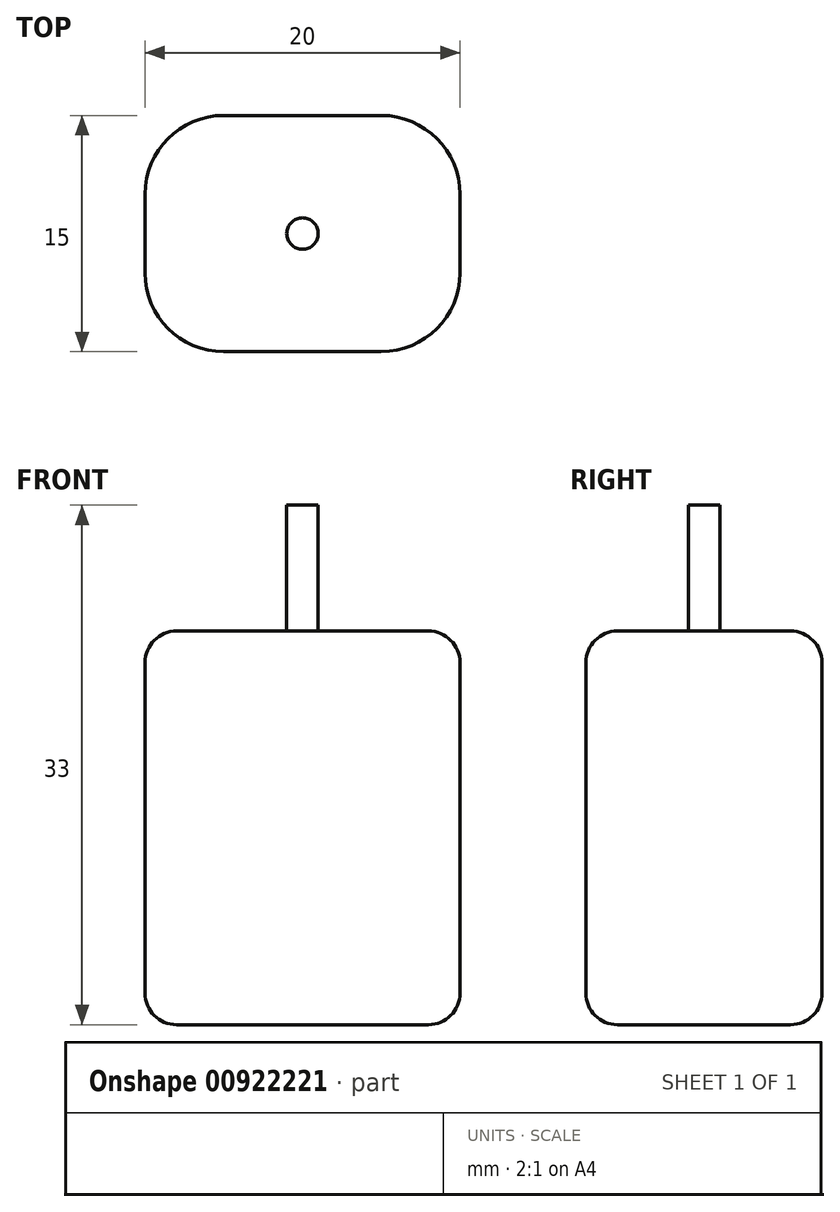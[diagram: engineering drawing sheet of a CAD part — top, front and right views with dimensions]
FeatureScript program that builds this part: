
annotation { "Feature Type Name" : "Feature", "Feature Type Description" : "" }
export const myFeature = defineFeature(function(context is Context, id is Id, definition is map)
    precondition{}
    {
        {
            var Q0;
            Q0=qCreatedBy(makeId("Top.planeOp"),FACE);
            var sketch = newSketch(context, id + "F0", { "sketchPlane" : qUnion([Q0])});
            skLineSegment(sketch, "E0.bottom", {"start": v(5, 7.5) * mm, "end": v(-5, 7.5) * mm});
            skLineSegment(sketch, "E0.top", {"start": v(5, -7.5) * mm, "end": v(-5, -7.5) * mm});
            skLineSegment(sketch, "E0.left", {"start": v(10, 2.5) * mm, "end": v(10, -2.5) * mm});
            skLineSegment(sketch, "E0.right", {"start": v(-10, 2.5) * mm, "end": v(-10, -2.5) * mm});
            skPoint(sketch, "E0.middle", {"position": v(0, 0) * mm});
            skPoint(sketch, "E1.visualSharp", {"position": v(-10, 7.5) * mm});
            skArc(sketch, "E1.filletArc", {"start": v(-5, 7.5) * mm, "mid": v(-8.54, 6.04) * mm, "end": v(-10, 2.5) * mm});
            skPoint(sketch, "E2.visualSharp", {"position": v(-10, -7.5) * mm});
            skArc(sketch, "E2.filletArc", {"start": v(-10, -2.5) * mm, "mid": v(-8.54, -6.04) * mm, "end": v(-5, -7.5) * mm});
            skPoint(sketch, "E3.visualSharp", {"position": v(10, -7.5) * mm});
            skArc(sketch, "E3.filletArc", {"start": v(5, -7.5) * mm, "mid": v(8.54, -6.04) * mm, "end": v(10, -2.5) * mm});
            skPoint(sketch, "E4.visualSharp", {"position": v(10, 7.5) * mm});
            skArc(sketch, "E4.filletArc", {"start": v(10, 2.5) * mm, "mid": v(8.54, 6.04) * mm, "end": v(5, 7.5) * mm});
            skSolve(sketch);
        }
        {
            var Q0;
            Q0 = qSketchRegion(id + "F0", true);
            extrude(context, id + "F1", {"entities" : qUnion([Q0]), "depth" : 25 * mm, "offsetDistance" : 25 * mm});
        }
        {
            var Q0;
            Q0=makeQuery(id+"F1.opExtrude","CAP_EDGE",EDGE,{"disambiguationData":[OSD([sQuery(id+"F0.wireOp",EDGE,"E0.bottom")])],"isStart":false});
            var Q1;
            Q1=makeQuery(id+"F1.opExtrude","CAP_EDGE",EDGE,{"disambiguationData":[OSD([sQuery(id+"F0.wireOp",EDGE,"E0.bottom")])],"isStart":true});
            fillet(context, id + "F2", {"entities" : qUnion([Q0, Q1]), "radius" : 2 * mm, "tangentPropagation" : true, "allowEdgeOverflow" : false});
        }
        {
            var Q0;
            Q0=makeQuery(id+"F1.opExtrude","CAP_FACE",FACE,{"disambiguationData":[OSD([sQuery(id+"F0.wireOp",EDGE,"E0.bottom"),sQuery(id+"F0.wireOp",EDGE,"E0.top"),sQuery(id+"F0.wireOp",EDGE,"E0.left"),sQuery(id+"F0.wireOp",EDGE,"E0.right"),sQuery(id+"F0.wireOp",EDGE,"E1.filletArc"),sQuery(id+"F0.wireOp",EDGE,"E2.filletArc"),sQuery(id+"F0.wireOp",EDGE,"E3.filletArc"),sQuery(id+"F0.wireOp",EDGE,"E4.filletArc")])],"isStart":false});
            var sketch = newSketch(context, id + "F3", { "sketchPlane" : qUnion([Q0])});
            skCircle(sketch, "E5", {"center": v(0, 0) * mm, "radius": 1 * mm});
            skSolve(sketch);
        }
        {
            var Q0;
            Q0 = qSketchRegion(id + "F3", true);
            extrude(context, id + "F4", {"entities" : qUnion([Q0]), "operationType" : NewBodyOperationType.ADD, "depth" : 8 * mm, "offsetDistance" : 25 * mm});
        }
    });
